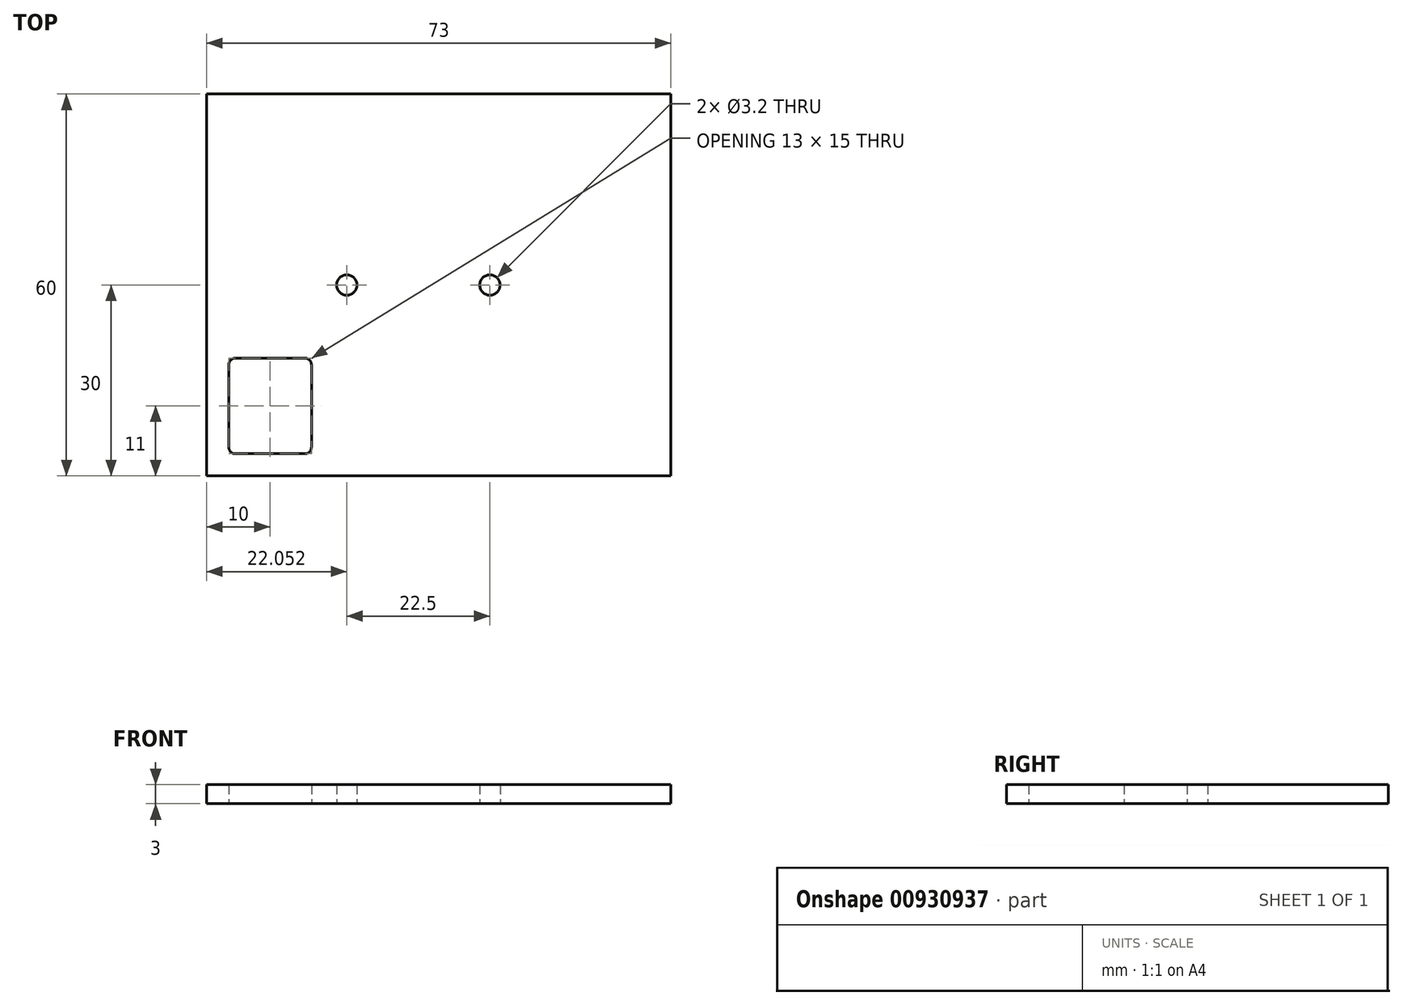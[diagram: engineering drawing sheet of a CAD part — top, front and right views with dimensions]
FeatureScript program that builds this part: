
annotation { "Feature Type Name" : "Feature", "Feature Type Description" : "" }
export const myFeature = defineFeature(function(context is Context, id is Id, definition is map)
    precondition{}
    {
        {
            var Q0;
            Q0=qCreatedBy(makeId("Top.planeOp"),FACE);
            var sketch = newSketch(context, id + "F0", { "sketchPlane" : qUnion([Q0])});
            skLineSegment(sketch, "E0.bottom", {"start": v(-73, -60) * mm, "end": v(0, -60) * mm});
            skLineSegment(sketch, "E0.top", {"start": v(-73, 0) * mm, "end": v(0, 0) * mm});
            skLineSegment(sketch, "E0.left", {"start": v(-73, -60) * mm, "end": v(-73, 0) * mm});
            skLineSegment(sketch, "E0.right", {"start": v(0, -60) * mm, "end": v(0, 0) * mm});
            skCircle(sketch, "E1", {"center": v(-50.95, -30) * mm, "radius": 1.6 * mm});
            skCircle(sketch, "E2", {"center": v(-28.45, -30) * mm, "radius": 1.6 * mm});
            skCircle(sketch, "E3", {"center": v(-28.45, -30) * mm, "radius": 18.25 * mm, "construction": true});
            skCircle(sketch, "E4", {"center": v(-50.95, -30) * mm, "radius": 18.25 * mm, "construction": true});
            skCircle(sketch, "E5", {"center": v(-50.95, -30) * mm, "radius": 4.25 * mm, "construction": true});
            skCircle(sketch, "E6", {"center": v(-63, -49) * mm, "radius": 4.25 * mm, "construction": true});
            skLineSegment(sketch, "E7.bottom", {"start": v(-69.5, -56.5) * mm, "end": v(-56.5, -56.5) * mm});
            skLineSegment(sketch, "E7.top", {"start": v(-69.5, -41.5) * mm, "end": v(-56.5, -41.5) * mm});
            skLineSegment(sketch, "E7.left", {"start": v(-69.5, -56.5) * mm, "end": v(-69.5, -41.5) * mm});
            skLineSegment(sketch, "E7.right", {"start": v(-56.5, -56.5) * mm, "end": v(-56.5, -41.5) * mm});
            skLineSegment(sketch, "E8", {"start": v(-69.5, -41.5) * mm, "end": v(-56.5, -56.5) * mm, "construction": true});
            skSolve(sketch);
        }
        {
            var Q0;
            Q0=qSketchRegion(id+"F0",true);
            extrude(context, id + "F1", {"entities" : qUnion([Q0]), "depth" : 3 * mm, "offsetDistance" : 25 * mm});
        }
        {
            var Q0;
            Q0=makeQuery(id+"F1.opExtrude","SWEPT_EDGE",EDGE,{"disambiguationData":[OSD([sQuery(id+"F0.wireOp",EDGE,"E7.top"),sQuery(id+"F0.wireOp",EDGE,"E7.left")])]});
            var Q1;
            Q1=makeQuery(id+"F1.opExtrude","SWEPT_EDGE",EDGE,{"disambiguationData":[OSD([sQuery(id+"F0.wireOp",EDGE,"E7.bottom"),sQuery(id+"F0.wireOp",EDGE,"E7.right")])]});
            var Q2;
            Q2=makeQuery(id+"F1.opExtrude","SWEPT_EDGE",EDGE,{"disambiguationData":[OSD([sQuery(id+"F0.wireOp",EDGE,"E7.bottom"),sQuery(id+"F0.wireOp",EDGE,"E7.left")])]});
            var Q3;
            Q3=makeQuery(id+"F1.opExtrude","SWEPT_EDGE",EDGE,{"disambiguationData":[OSD([sQuery(id+"F0.wireOp",EDGE,"E7.top"),sQuery(id+"F0.wireOp",EDGE,"E7.right")])]});
            fillet(context, id + "F2", {"entities" : qUnion([Q0, Q1, Q2, Q3]), "radius" : 1 * mm, "tangentPropagation" : true, "allowEdgeOverflow" : false});
        }
    });
